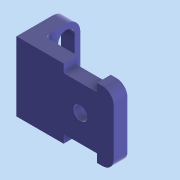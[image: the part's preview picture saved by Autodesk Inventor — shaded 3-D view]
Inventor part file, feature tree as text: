
AUTODESK INVENTOR PART (.ipt)
format: ipt  version: 2018 (Build 220112000, 112)  size: 169,472 bytes
history: native  units: mm
features: extrude x4, sketch x4, fillet x3
ambient origin geometry x8: Origin, YZ Plane, XZ Plane, XY Plane, X Axis, Y Axis, Z Axis, Center Point
bodies: Solid1 (feature_tree)
feature tree (11):
  extrude  "Extrusion1"  Depth=25.0mm
  extrude  "Extrusion2"  Depth=12.0mm
  extrude  "Extrusion3"  Depth=19.0mm
  extrude  "Extrusion4"  Depth=5.0mm TaperAngle=0.0deg
  fillet  "Fillet1"  Radius=18.0mm
  fillet  "Fillet2"  Radius=25.0mm
  fillet  "Fillet3"  Radius=5.0mm
  sketch  "Sketch1"  dims[d0=35.0mm d1=25.0mm]
  sketch  "Sketch2"  dims[d2=6.0mm d3=12.0mm]
  sketch  "Sketch3"  dims[d4=6.0mm d5=19.0mm]
  sketch  "Sketch4"  dims[d6=8.0mm d7=5.0mm d8=0.0mm d9=18.0mm d10=25.0mm d11=5.0mm d12=0.0mm d16=12.5mm d17=15.0mm d18=5.0mm d19=3.0mm d20=5.0mm d21=0.0mm d22=5.0mm d23=3.0mm d24=0.0mm d25=5.0mm d26=2.0mm d27=4.0mm]
